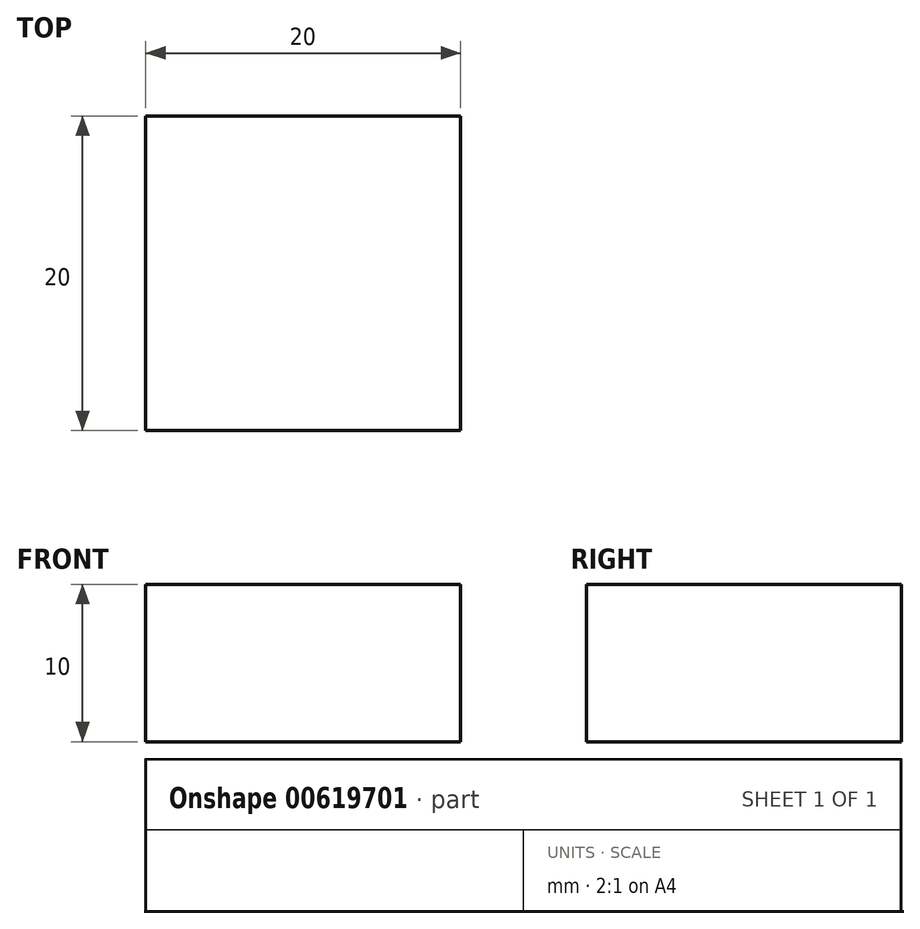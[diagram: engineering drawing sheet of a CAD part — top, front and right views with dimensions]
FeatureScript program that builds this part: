
annotation { "Feature Type Name" : "Feature", "Feature Type Description" : "" }
export const myFeature = defineFeature(function(context is Context, id is Id, definition is map)
    precondition{}
    {
        {
            var Q0;
            Q0=qCreatedBy(makeId("Top.planeOp"),FACE);
            var sketch = newSketch(context, id + "F0", { "sketchPlane" : qUnion([Q0])});
            skLineSegment(sketch, "E0.bottom", {"start": v(10, -10) * mm, "end": v(-10, -10) * mm});
            skLineSegment(sketch, "E0.top", {"start": v(10, 10) * mm, "end": v(-10, 10) * mm});
            skLineSegment(sketch, "E0.left", {"start": v(10, -10) * mm, "end": v(10, 10) * mm});
            skLineSegment(sketch, "E0.right", {"start": v(-10, -10) * mm, "end": v(-10, 10) * mm});
            skPoint(sketch, "E0.middle", {"position": v(0, 0) * mm});
            skSolve(sketch);
        }
        {
            var Q0;
            Q0 = qSketchRegion(id + "F0", true);
            extrude(context, id + "F1", {"entities" : qUnion([Q0]), "depth" : 10 * mm, "offsetDistance" : 25 * mm});
        }
    });
